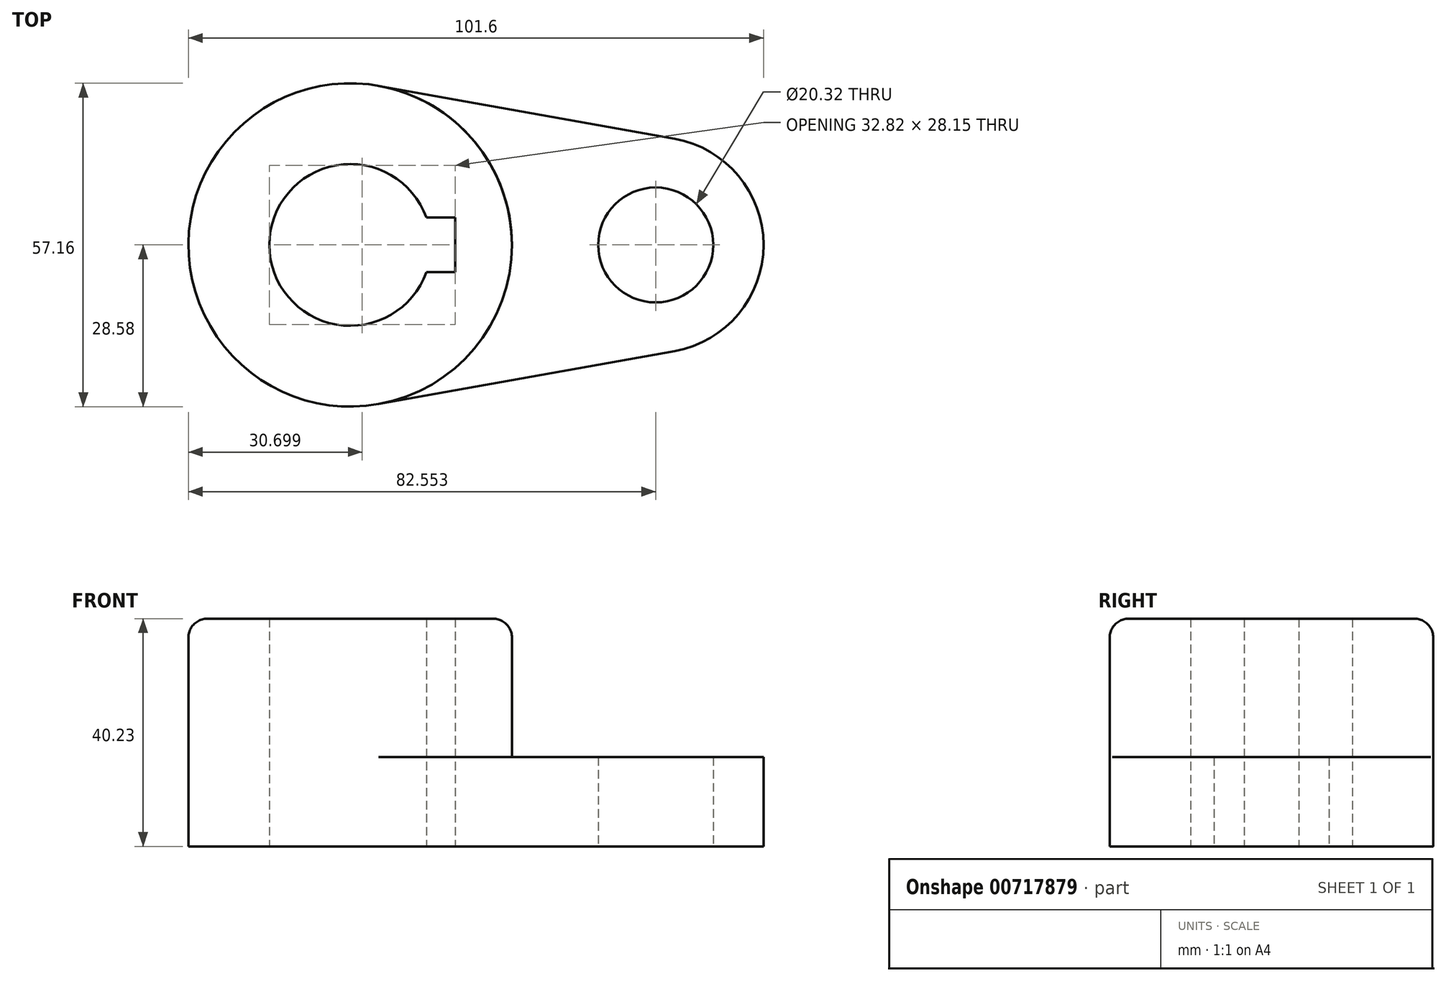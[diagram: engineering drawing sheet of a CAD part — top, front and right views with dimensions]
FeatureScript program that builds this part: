
annotation { "Feature Type Name" : "Feature", "Feature Type Description" : "" }
export const myFeature = defineFeature(function(context is Context, id is Id, definition is map)
    precondition{}
    {
        {
            var Q0;
            Q0=qCreatedBy(makeId("Top.planeOp"),FACE);
            var sketch = newSketch(context, id + "F0", { "sketchPlane" : qUnion([Q0])});
            skArc(sketch, "E0", {"start": v(33.33, -18.75) * mm, "mid": v(49.01, 0) * mm, "end": v(33.33, 18.75) * mm});
            skCircle(sketch, "E1", {"center": v(29.96, 0) * mm, "radius": 10.16 * mm});
            skArc(sketch, "E2", {"start": v(-10.56, 4.83) * mm, "mid": v(-38.3, 0) * mm, "end": v(-10.56, -4.83) * mm});
            skCircle(sketch, "E3", {"center": v(-24.01, 0) * mm, "radius": 28.58 * mm});
            skLineSegment(sketch, "E4", {"start": v(-18.97, 28.13) * mm, "end": v(33.33, 18.75) * mm});
            skLineSegment(sketch, "E5", {"start": v(-18.97, -28.13) * mm, "end": v(33.33, -18.75) * mm});
            skLineSegment(sketch, "E6", {"start": v(-5.48, 0) * mm, "end": v(-5.48, 4.83) * mm});
            skLineSegment(sketch, "E7", {"start": v(-5.48, 4.83) * mm, "end": v(-10.56, 4.83) * mm});
            skLineSegment(sketch, "E8", {"start": v(-5.48, 0) * mm, "end": v(-5.48, -4.83) * mm});
            skLineSegment(sketch, "E9", {"start": v(-5.48, -4.83) * mm, "end": v(-10.56, -4.83) * mm});
            skSolve(sketch);
        }
        {
            var Q0;
            Q0=makeQuery(id+"F0.imprint","IMPRINT",FACE,{"disambiguationData":[TD([[makeQuery(id+"F0.imprint","IMPRINT",EDGE,{"derivedFrom":sQuery(id+"F0.wireOp",EDGE,"E2")}),-1.0]])]});
            extrude(context, id + "F1", {"entities" : qUnion([Q0]), "depth" : 40.23 * mm, "offsetDistance" : 25.4 * mm});
        }
        {
            var Q0;
            Q0=makeQuery(id+"F0.imprint","IMPRINT",FACE,{"disambiguationData":[TD([[makeQuery(id+"F0.imprint","IMPRINT",EDGE,{"derivedFrom":sQuery(id+"F0.wireOp",EDGE,"E0")}),1.0]])]});
            extrude(context, id + "F2", {"entities" : qUnion([Q0]), "operationType" : NewBodyOperationType.ADD, "depth" : 15.77 * mm, "offsetDistance" : 25.4 * mm});
        }
        {
            var Q0;
            Q0=makeQuery(id+"F1.opExtrude","CAP_EDGE",EDGE,{"disambiguationData":[OSD([sQuery(id+"F0.wireOp",EDGE,"E3")])],"isStart":false});
            fillet(context, id + "F3", {"entities" : qUnion([Q0]), "radius" : 3.3 * mm, "tangentPropagation" : true, "allowEdgeOverflow" : false});
        }
    });
